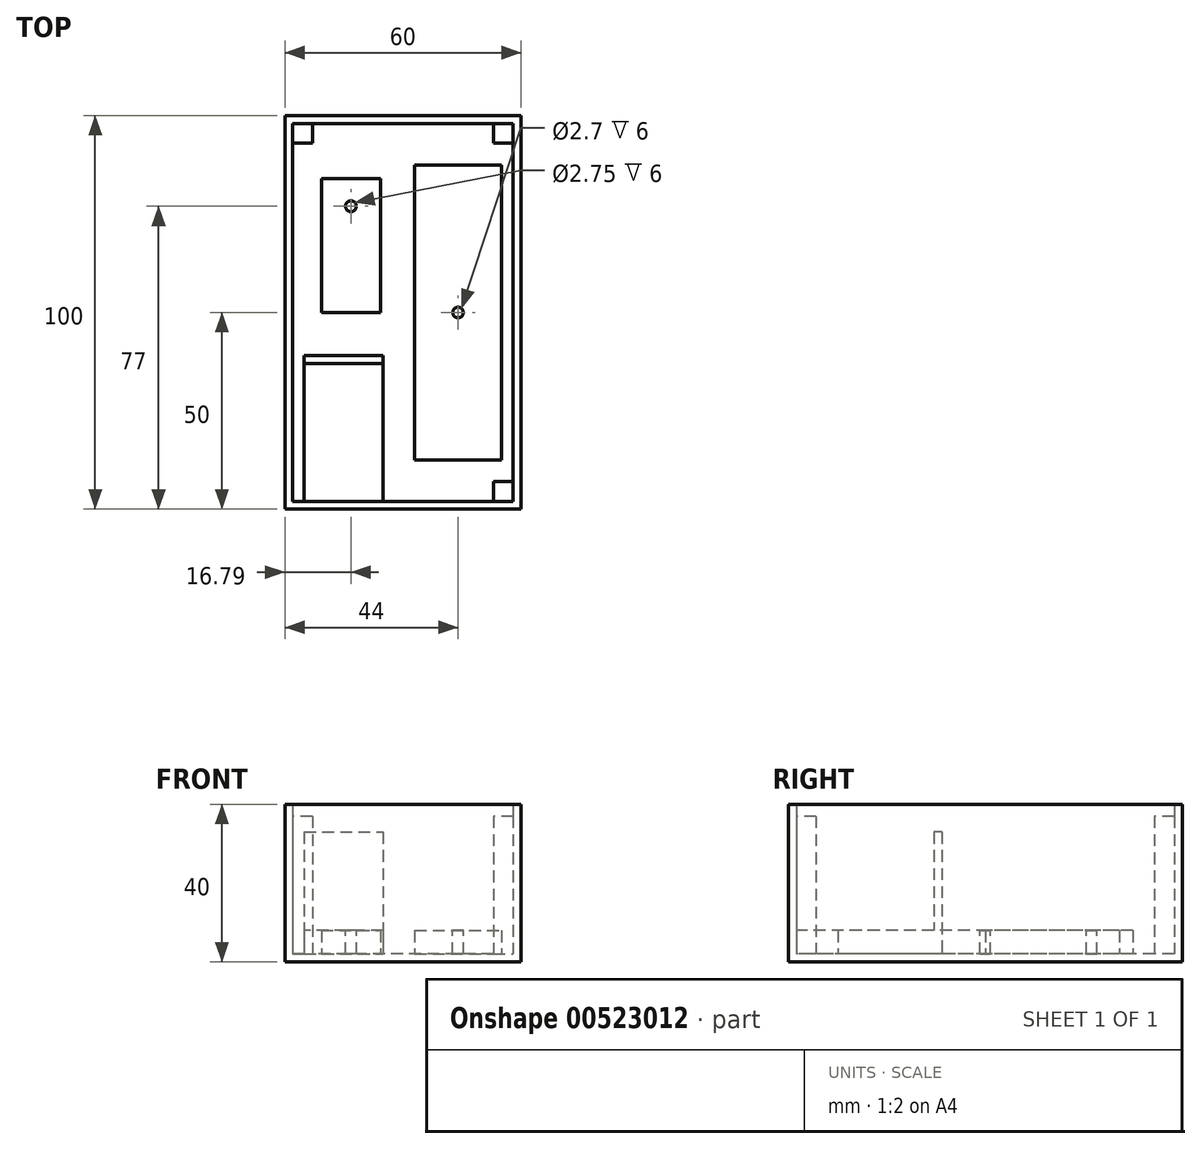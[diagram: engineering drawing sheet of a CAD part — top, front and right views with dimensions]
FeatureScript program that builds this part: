
annotation { "Feature Type Name" : "Feature", "Feature Type Description" : "" }
export const myFeature = defineFeature(function(context is Context, id is Id, definition is map)
    precondition{}
    {
        {
            var Q0;
            Q0=qCreatedBy(makeId("Top.planeOp"),FACE);
            var sketch = newSketch(context, id + "F0", { "sketchPlane" : qUnion([Q0])});
            skLineSegment(sketch, "E0.bottom", {"start": v(30, 50) * mm, "end": v(-30, 50) * mm});
            skLineSegment(sketch, "E0.top", {"start": v(30, -50) * mm, "end": v(-30, -50) * mm});
            skLineSegment(sketch, "E0.left", {"start": v(30, 50) * mm, "end": v(30, -50) * mm});
            skLineSegment(sketch, "E0.right", {"start": v(-30, 50) * mm, "end": v(-30, -50) * mm});
            skPoint(sketch, "E0.middle", {"position": v(0, 0) * mm});
            skSolve(sketch);
        }
        {
            var Q0;
            Q0=makeQuery(id+"F0.imprint","IMPRINT",FACE,{"disambiguationData":[TD([[makeQuery(id+"F0.imprint","IMPRINT",EDGE,{"derivedFrom":sQuery(id+"F0.wireOp",EDGE,"E0.bottom")}),1.0]])]});
            extrude(context, id + "F1", {"entities" : qUnion([Q0]), "depth" : 40 * mm, "offsetDistance" : 25 * mm});
        }
        {
            var Q0;
            Q0=makeQuery(id+"F1.opExtrude","CAP_FACE",FACE,{"disambiguationData":[OSD([sQuery(id+"F0.wireOp",EDGE,"E0.bottom"),sQuery(id+"F0.wireOp",EDGE,"E0.top"),sQuery(id+"F0.wireOp",EDGE,"E0.left"),sQuery(id+"F0.wireOp",EDGE,"E0.right")])],"isStart":false});
            shell(context, id + "F2", {"entities" : qUnion([Q0]), "thickness" : 2 * mm});
        }
        {
            var Q0;
            Q0=makeQuery(id+"F2.opShell","OFFSET_FACE",FACE,{"disambiguationData":[OSD([sQuery(id+"F0.wireOp",EDGE,"E0.bottom"),sQuery(id+"F0.wireOp",EDGE,"E0.top"),sQuery(id+"F0.wireOp",EDGE,"E0.left"),sQuery(id+"F0.wireOp",EDGE,"E0.right")])]});
            var sketch = newSketch(context, id + "F3", { "sketchPlane" : qUnion([Q0])});
            skLineSegment(sketch, "E1.bottom", {"start": v(3, 37.5) * mm, "end": v(25, 37.5) * mm});
            skLineSegment(sketch, "E1.top", {"start": v(3, -37.5) * mm, "end": v(25, -37.5) * mm});
            skLineSegment(sketch, "E1.left", {"start": v(3, 37.5) * mm, "end": v(3, -37.5) * mm});
            skLineSegment(sketch, "E1.right", {"start": v(25, 37.5) * mm, "end": v(25, -37.5) * mm});
            skLineSegment(sketch, "E2", {"start": v(28, 0) * mm, "end": v(-28, 0) * mm, "construction": true});
            skPoint(sketch, "E3", {"position": v(3, 0) * mm});
            skSolve(sketch);
        }
        {
            var Q0;
            Q0=makeQuery(id+"F3.imprint","IMPRINT",FACE,{"disambiguationData":[TD([[makeQuery(id+"F3.imprint","IMPRINT",EDGE,{"derivedFrom":sQuery(id+"F3.wireOp",EDGE,"E1.bottom")}),-1.0]])]});
            extrude(context, id + "F4", {"entities" : qUnion([Q0]), "operationType" : NewBodyOperationType.ADD, "depth" : 6 * mm, "offsetDistance" : 25 * mm});
        }
        {
            var Q0;
            Q0=makeQuery(id+"F4.opExtrude","CAP_FACE",FACE,{"disambiguationData":[OSD([sQuery(id+"F3.wireOp",EDGE,"E1.bottom"),sQuery(id+"F3.wireOp",EDGE,"E1.top"),sQuery(id+"F3.wireOp",EDGE,"E1.left"),sQuery(id+"F3.wireOp",EDGE,"E1.right")])],"isStart":false});
            var sketch = newSketch(context, id + "F5", { "sketchPlane" : qUnion([Q0])});
            skCircle(sketch, "E4", {"center": v(14, 0) * mm, "radius": 1.35 * mm});
            skPoint(sketch, "E4.centerSnap0", {"position": v(14, 37.5) * mm});
            skSolve(sketch);
        }
        {
            var Q0;
            Q0=makeQuery(id+"F5.imprint","IMPRINT",FACE,{"disambiguationData":[TD([[makeQuery(id+"F5.imprint","IMPRINT",EDGE,{"derivedFrom":sQuery(id+"F5.wireOp",EDGE,"E4")}),1.0]])]});
            var Q1;
            Q1=sQuery(id+"F5.wireOp",EDGE,"E4");
            extrude(context, id + "F6", {"entities" : qUnion([Q0]), "operationType" : NewBodyOperationType.REMOVE, "surfaceEntities" : qUnion([Q1]), "oppositeDirection" : true, "depth" : 6 * mm, "offsetDistance" : 25 * mm});
        }
        {
            var Q0;
            Q0=makeQuery(id+"F2.opShell","OFFSET_FACE",FACE,{"disambiguationData":[OSD([sQuery(id+"F0.wireOp",EDGE,"E0.bottom"),sQuery(id+"F0.wireOp",EDGE,"E0.top"),sQuery(id+"F0.wireOp",EDGE,"E0.left"),sQuery(id+"F0.wireOp",EDGE,"E0.right")])]});
            var sketch = newSketch(context, id + "F7", { "sketchPlane" : qUnion([Q0])});
            skLineSegment(sketch, "E5.bottom", {"start": v(-25.1, -11) * mm, "end": v(-5.1, -11) * mm});
            skLineSegment(sketch, "E5.top", {"start": v(-25.1, -48) * mm, "end": v(-5.1, -48) * mm});
            skLineSegment(sketch, "E5.left", {"start": v(-25.1, -11) * mm, "end": v(-25.1, -48) * mm});
            skLineSegment(sketch, "E5.right", {"start": v(-5.1, -11) * mm, "end": v(-5.1, -48) * mm});
            skSolve(sketch);
        }
        {
            var Q0;
            Q0=makeQuery(id+"F7.imprint","IMPRINT",FACE,{"disambiguationData":[TD([[makeQuery(id+"F7.imprint","IMPRINT",EDGE,{"derivedFrom":sQuery(id+"F7.wireOp",EDGE,"E5.bottom")}),-1.0]])]});
            extrude(context, id + "F8", {"entities" : qUnion([Q0]), "operationType" : NewBodyOperationType.ADD, "depth" : 6 * mm, "offsetDistance" : 25 * mm});
        }
        {
            var Q0;
            Q0=makeQuery(id+"F8.opExtrude","CAP_FACE",FACE,{"disambiguationData":[OSD([sQuery(id+"F7.wireOp",EDGE,"E5.bottom"),sQuery(id+"F7.wireOp",EDGE,"E5.top"),sQuery(id+"F7.wireOp",EDGE,"E5.left"),sQuery(id+"F7.wireOp",EDGE,"E5.right")])],"isStart":false});
            var sketch = newSketch(context, id + "F9", { "sketchPlane" : qUnion([Q0])});
            skLineSegment(sketch, "E6.bottom", {"start": v(-25.1, -11) * mm, "end": v(-5.1, -11) * mm});
            skLineSegment(sketch, "E6.top", {"start": v(-25.1, -13) * mm, "end": v(-5.1, -13) * mm});
            skLineSegment(sketch, "E6.left", {"start": v(-25.1, -13) * mm, "end": v(-25.1, -11) * mm});
            skLineSegment(sketch, "E6.right", {"start": v(-5.1, -13) * mm, "end": v(-5.1, -11) * mm});
            skSolve(sketch);
        }
        {
            var Q0;
            Q0=makeQuery(id+"F9.imprint","IMPRINT",FACE,{"disambiguationData":[TD([[makeQuery(id+"F9.imprint","IMPRINT",EDGE,{"derivedFrom":sQuery(id+"F9.wireOp",EDGE,"E6.bottom")}),-1.0]])]});
            extrude(context, id + "F10", {"entities" : qUnion([Q0]), "operationType" : NewBodyOperationType.ADD, "depth" : 25 * mm, "offsetDistance" : 25 * mm});
        }
        {
            var Q0;
            Q0=makeQuery(id+"F2.opShell","OFFSET_FACE",FACE,{"disambiguationData":[OSD([sQuery(id+"F0.wireOp",EDGE,"E0.bottom"),sQuery(id+"F0.wireOp",EDGE,"E0.top"),sQuery(id+"F0.wireOp",EDGE,"E0.left"),sQuery(id+"F0.wireOp",EDGE,"E0.right")])]});
            var sketch = newSketch(context, id + "F11", { "sketchPlane" : qUnion([Q0])});
            skLineSegment(sketch, "E7.bottom", {"start": v(-20.71, 34) * mm, "end": v(-5.71, 34) * mm});
            skLineSegment(sketch, "E7.top", {"start": v(-20.71, 0) * mm, "end": v(-5.71, 0) * mm});
            skLineSegment(sketch, "E7.left", {"start": v(-20.71, 34) * mm, "end": v(-20.71, 0) * mm});
            skLineSegment(sketch, "E7.right", {"start": v(-5.71, 34) * mm, "end": v(-5.71, 0) * mm});
            skSolve(sketch);
        }
        {
            var Q0;
            Q0=makeQuery(id+"F11.imprint","IMPRINT",FACE,{"disambiguationData":[TD([[makeQuery(id+"F11.imprint","IMPRINT",EDGE,{"derivedFrom":sQuery(id+"F11.wireOp",EDGE,"E7.bottom")}),-1.0]])]});
            extrude(context, id + "F12", {"entities" : qUnion([Q0]), "operationType" : NewBodyOperationType.ADD, "depth" : 6 * mm, "offsetDistance" : 25 * mm});
        }
        {
            var Q0;
            Q0=makeQuery(id+"F12.opExtrude","CAP_FACE",FACE,{"disambiguationData":[OSD([sQuery(id+"F11.wireOp",EDGE,"E7.bottom"),sQuery(id+"F11.wireOp",EDGE,"E7.top"),sQuery(id+"F11.wireOp",EDGE,"E7.left"),sQuery(id+"F11.wireOp",EDGE,"E7.right")])],"isStart":false});
            var sketch = newSketch(context, id + "F13", { "sketchPlane" : qUnion([Q0])});
            skPoint(sketch, "E8.centerSnap0", {"position": v(-13.21, 34) * mm});
            skPoint(sketch, "E8.centerSnap1", {"position": v(-20.71, 17) * mm});
            skCircle(sketch, "E9", {"center": v(-13.21, 27) * mm, "radius": 1.38 * mm});
            skSolve(sketch);
        }
        {
            var Q0;
            Q0=makeQuery(id+"F13.imprint","IMPRINT",FACE,{"disambiguationData":[TD([[makeQuery(id+"F13.imprint","IMPRINT",EDGE,{"derivedFrom":sQuery(id+"F13.wireOp",EDGE,"E9")}),1.0]])]});
            extrude(context, id + "F14", {"entities" : qUnion([Q0]), "operationType" : NewBodyOperationType.REMOVE, "oppositeDirection" : true, "depth" : 6 * mm, "offsetDistance" : 25 * mm});
        }
        {
            var Q0;
            Q0=makeQuery(id+"F2.opShell","OFFSET_FACE",FACE,{"disambiguationData":[OSD([sQuery(id+"F0.wireOp",EDGE,"E0.bottom"),sQuery(id+"F0.wireOp",EDGE,"E0.top"),sQuery(id+"F0.wireOp",EDGE,"E0.left"),sQuery(id+"F0.wireOp",EDGE,"E0.right")])]});
            var sketch = newSketch(context, id + "F15", { "sketchPlane" : qUnion([Q0])});
            skLineSegment(sketch, "E10.bottom", {"start": v(-28, 48) * mm, "end": v(-23, 48) * mm});
            skLineSegment(sketch, "E10.top", {"start": v(-28, 43) * mm, "end": v(-23, 43) * mm});
            skLineSegment(sketch, "E10.left", {"start": v(-28, 48) * mm, "end": v(-28, 43) * mm});
            skLineSegment(sketch, "E10.right", {"start": v(-23, 48) * mm, "end": v(-23, 43) * mm});
            skLineSegment(sketch, "E11.bottom", {"start": v(23, 48) * mm, "end": v(28, 48) * mm});
            skLineSegment(sketch, "E11.top", {"start": v(23, 43) * mm, "end": v(28, 43) * mm});
            skLineSegment(sketch, "E11.left", {"start": v(23, 48) * mm, "end": v(23, 43) * mm});
            skLineSegment(sketch, "E11.right", {"start": v(28, 48) * mm, "end": v(28, 43) * mm});
            skLineSegment(sketch, "E12.bottom", {"start": v(23, -43) * mm, "end": v(28, -43) * mm});
            skLineSegment(sketch, "E12.top", {"start": v(23, -48) * mm, "end": v(28, -48) * mm});
            skLineSegment(sketch, "E12.left", {"start": v(23, -43) * mm, "end": v(23, -48) * mm});
            skLineSegment(sketch, "E12.right", {"start": v(28, -43) * mm, "end": v(28, -48) * mm});
            skSolve(sketch);
        }
        {
            var Q0;
            Q0=makeQuery(id+"F15.imprint","IMPRINT",FACE,{"disambiguationData":[TD([[makeQuery(id+"F15.imprint","IMPRINT",EDGE,{"derivedFrom":sQuery(id+"F15.wireOp",EDGE,"E10.bottom")}),1.0]])]});
            var Q1;
            Q1=makeQuery(id+"F15.imprint","IMPRINT",FACE,{"disambiguationData":[TD([[makeQuery(id+"F15.imprint","IMPRINT",EDGE,{"derivedFrom":sQuery(id+"F15.wireOp",EDGE,"E11.bottom")}),1.0]])]});
            var Q2;
            Q2=makeQuery(id+"F15.imprint","IMPRINT",FACE,{"disambiguationData":[TD([[makeQuery(id+"F15.imprint","IMPRINT",EDGE,{"derivedFrom":sQuery(id+"F15.wireOp",EDGE,"E12.bottom")}),-1.0]])]});
            extrude(context, id + "F16", {"entities" : qUnion([Q0, Q1, Q2]), "operationType" : NewBodyOperationType.ADD, "depth" : 35 * mm, "offsetDistance" : 25 * mm});
        }
    });
